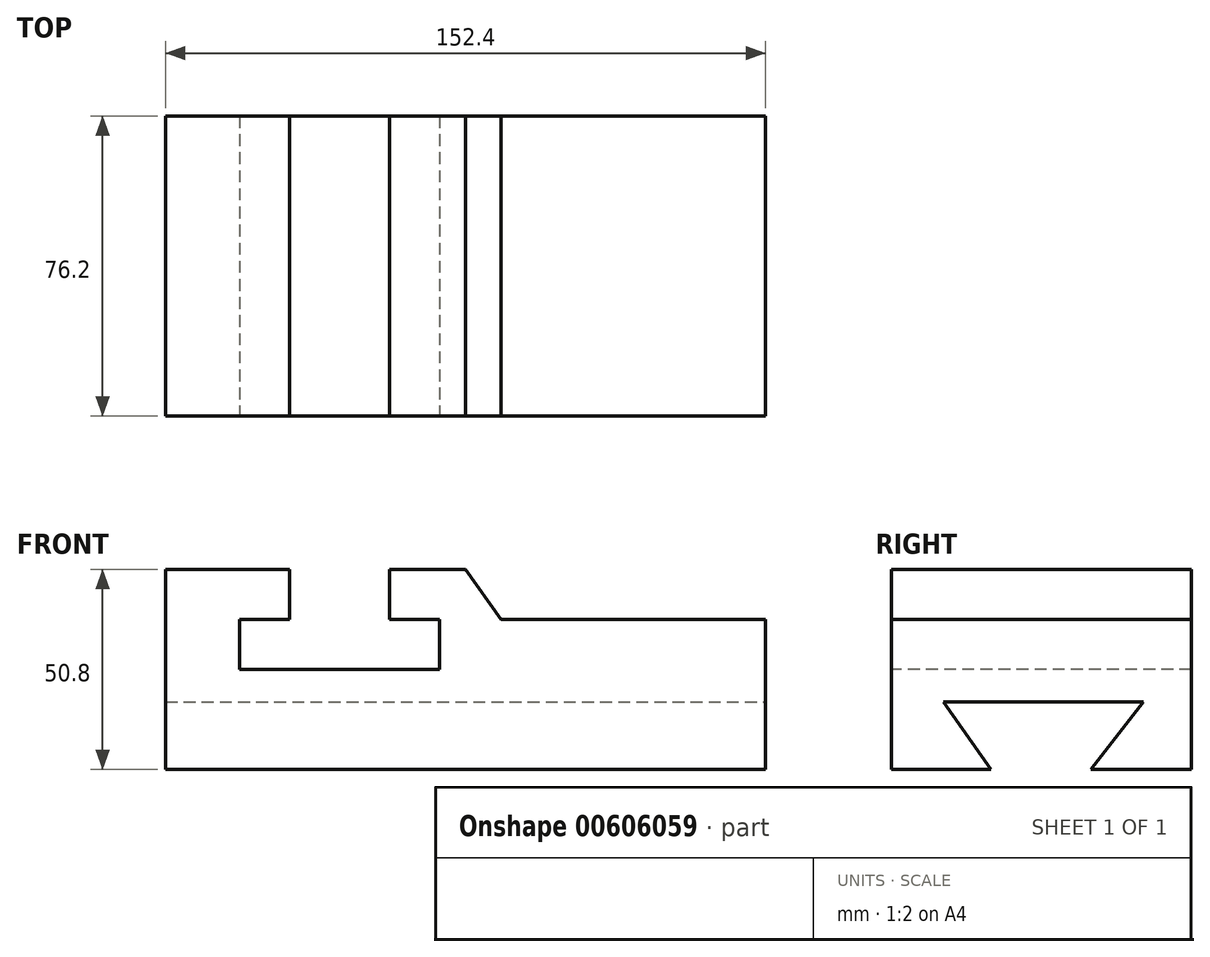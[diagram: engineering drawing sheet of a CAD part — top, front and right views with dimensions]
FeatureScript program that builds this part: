
annotation { "Feature Type Name" : "Feature", "Feature Type Description" : "" }
export const myFeature = defineFeature(function(context is Context, id is Id, definition is map)
    precondition{}
    {
        {
            var Q0;
            Q0=qCreatedBy(makeId("Front.planeOp"),FACE);
            var sketch = newSketch(context, id + "F0", { "sketchPlane" : qUnion([Q0])});
            skLineSegment(sketch, "E0", {"start": v(0, 0) * mm, "end": v(152.4, 0) * mm});
            skLineSegment(sketch, "E1", {"start": v(152.4, 0) * mm, "end": v(152.4, 38.1) * mm});
            skLineSegment(sketch, "E2", {"start": v(152.4, 38.1) * mm, "end": v(85.15, 38.1) * mm});
            skLineSegment(sketch, "E3", {"start": v(85.15, 38.1) * mm, "end": v(76.2, 50.8) * mm});
            skLineSegment(sketch, "E4", {"start": v(76.2, 50.8) * mm, "end": v(0, 50.8) * mm});
            skLineSegment(sketch, "E5", {"start": v(0, 50.8) * mm, "end": v(0, 0) * mm});
            skSolve(sketch);
        }
        {
            var Q0;
            Q0 = qSketchRegion(id + "F0", true);
            extrude(context, id + "F1", {"entities" : qUnion([Q0]), "oppositeDirection" : true, "depth" : 76.2 * mm, "offsetDistance" : 25.4 * mm});
        }
        {
            var Q0;
            Q0=makeQuery(id+"F1.opExtrude","CAP_FACE",FACE,{"disambiguationData":[OSD([sQuery(id+"F0.wireOp",EDGE,"E0"),sQuery(id+"F0.wireOp",EDGE,"E1"),sQuery(id+"F0.wireOp",EDGE,"E2"),sQuery(id+"F0.wireOp",EDGE,"E3"),sQuery(id+"F0.wireOp",EDGE,"E4"),sQuery(id+"F0.wireOp",EDGE,"E5")])],"isStart":true});
            var sketch = newSketch(context, id + "F2", { "sketchPlane" : qUnion([Q0])});
            skLineSegment(sketch, "E6", {"start": v(0, 50.8) * mm, "end": v(31.5, 50.8) * mm});
            skLineSegment(sketch, "E7", {"start": v(31.5, 50.8) * mm, "end": v(31.5, 38.1) * mm});
            skLineSegment(sketch, "E8", {"start": v(31.5, 38.1) * mm, "end": v(18.8, 38.1) * mm});
            skLineSegment(sketch, "E9", {"start": v(18.8, 38.1) * mm, "end": v(18.8, 25.4) * mm});
            skLineSegment(sketch, "E10", {"start": v(18.8, 25.4) * mm, "end": v(69.6, 25.4) * mm});
            skLineSegment(sketch, "E11", {"start": v(69.6, 25.4) * mm, "end": v(69.6, 38.1) * mm});
            skLineSegment(sketch, "E12", {"start": v(69.6, 38.1) * mm, "end": v(56.9, 38.1) * mm});
            skLineSegment(sketch, "E13", {"start": v(56.9, 38.1) * mm, "end": v(56.9, 50.8) * mm});
            skLineSegment(sketch, "E14", {"start": v(56.9, 50.8) * mm, "end": v(31.5, 50.8) * mm});
            skSolve(sketch);
        }
        {
            var Q0;
            Q0=makeQuery(id+"F2.imprint","IMPRINT",FACE,{"disambiguationData":[TD([[makeQuery(id+"F2.imprint","IMPRINT",EDGE,{"derivedFrom":sQuery(id+"F2.wireOp",EDGE,"E7")}),1.0]])]});
            extrude(context, id + "F3", {"entities" : qUnion([Q0]), "operationType" : NewBodyOperationType.REMOVE, "oppositeDirection" : true, "depth" : 76.2 * mm, "offsetDistance" : 25.4 * mm});
        }
        {
            var Q0;
            Q0=makeQuery(id+"F1.opExtrude","SWEPT_FACE",FACE,{"disambiguationData":[OSD([sQuery(id+"F0.wireOp",EDGE,"E1")])]});
            var sketch = newSketch(context, id + "F4", { "sketchPlane" : qUnion([Q0])});
            skLineSegment(sketch, "E15", {"start": v(13.16, 17.18) * mm, "end": v(63.96, 17.18) * mm});
            skLineSegment(sketch, "E16", {"start": v(25.31, 0) * mm, "end": v(50.71, 0) * mm});
            skLineSegment(sketch, "E17", {"start": v(50.71, 0) * mm, "end": v(63.96, 17.18) * mm});
            skLineSegment(sketch, "E18", {"start": v(25.31, 0) * mm, "end": v(13.16, 17.18) * mm});
            skSolve(sketch);
        }
        {
            var Q0;
            Q0=makeQuery(id+"F4.imprint","IMPRINT",FACE,{"disambiguationData":[TD([[makeQuery(id+"F4.imprint","IMPRINT",EDGE,{"derivedFrom":sQuery(id+"F4.wireOp",EDGE,"E15")}),-1.0]])]});
            extrude(context, id + "F5", {"entities" : qUnion([Q0]), "operationType" : NewBodyOperationType.REMOVE, "oppositeDirection" : true, "depth" : 152.4 * mm, "offsetDistance" : 25.4 * mm});
        }
    });
